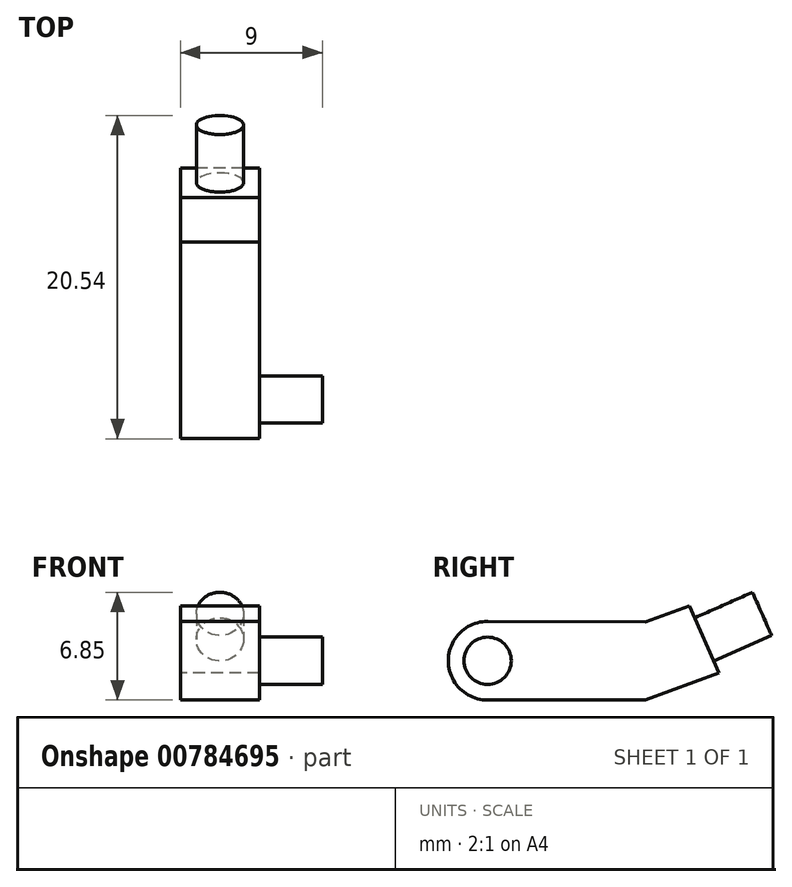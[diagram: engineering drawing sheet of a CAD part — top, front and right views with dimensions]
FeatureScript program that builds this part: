
annotation { "Feature Type Name" : "Feature", "Feature Type Description" : "" }
export const myFeature = defineFeature(function(context is Context, id is Id, definition is map)
    precondition{}
    {
        {
            var Q0;
            Q0=qCreatedBy(makeId("Right.planeOp"),FACE);
            var sketch = newSketch(context, id + "F0", { "sketchPlane" : qUnion([Q0])});
            skLineSegment(sketch, "E0", {"start": v(0, 0) * mm, "end": v(0, -5) * mm});
            skArc(sketch, "E1", {"start": v(0, 0) * mm, "mid": v(-2.5, -2.5) * mm, "end": v(0, -5) * mm});
            skLineSegment(sketch, "E2", {"start": v(0, 0) * mm, "end": v(10, -0.03) * mm});
            skLineSegment(sketch, "E3", {"start": v(0, -5) * mm, "end": v(10, -4.97) * mm});
            skLineSegment(sketch, "E4", {"start": v(10, -4.97) * mm, "end": v(14.7, -3.26) * mm});
            skLineSegment(sketch, "E5", {"start": v(10, -0.03) * mm, "end": v(12.83, 0.98) * mm});
            skLineSegment(sketch, "E6", {"start": v(12.83, 0.98) * mm, "end": v(14.7, -3.26) * mm});
            skSolve(sketch);
        }
        {
            var Q0;
            Q0=makeQuery(id+"F0.imprint","IMPRINT",FACE,{"disambiguationData":[TD([[makeQuery(id+"F0.imprint","IMPRINT",EDGE,{"derivedFrom":sQuery(id+"F0.wireOp",EDGE,"E0")}),1.0]])]});
            var Q1;
            Q1=makeQuery(id+"F0.imprint","IMPRINT",FACE,{"disambiguationData":[TD([[makeQuery(id+"F0.imprint","IMPRINT",EDGE,{"derivedFrom":sQuery(id+"F0.wireOp",EDGE,"E0")}),-1.0]])]});
            extrude(context, id + "F1", {"entities" : qUnion([Q0, Q1]), "depth" : 5 * mm, "offsetDistance" : 25 * mm});
        }
        {
            var Q0;
            Q0=makeQuery(id+"F1.opExtrude","SWEPT_FACE",FACE,{"disambiguationData":[OSD([sQuery(id+"F0.wireOp",EDGE,"E6")])]});
            var sketch = newSketch(context, id + "F2", { "sketchPlane" : qUnion([Q0])});
            skCircle(sketch, "E7", {"center": v(-2.5, -6.6) * mm, "radius": 1.5 * mm});
            skPoint(sketch, "E7.centerSnap0", {"position": v(0, -6.6) * mm});
            skPoint(sketch, "E7.centerSnap1", {"position": v(-2.5, -4.29) * mm});
            skSolve(sketch);
        }
        {
            var Q0;
            Q0=makeQuery(id+"F1.opExtrude","CAP_FACE",FACE,{"disambiguationData":[OSD([sQuery(id+"F0.wireOp",EDGE,"E1"),sQuery(id+"F0.wireOp",EDGE,"E2"),sQuery(id+"F0.wireOp",EDGE,"E3"),sQuery(id+"F0.wireOp",EDGE,"E4"),sQuery(id+"F0.wireOp",EDGE,"E5"),sQuery(id+"F0.wireOp",EDGE,"E6")])],"isStart":false});
            var sketch = newSketch(context, id + "F3", { "sketchPlane" : qUnion([Q0])});
            skCircle(sketch, "E8", {"center": v(0, -2.5) * mm, "radius": 1.5 * mm});
            skSolve(sketch);
        }
        {
            var Q0;
            Q0=makeQuery(id+"F3.imprint","IMPRINT",FACE,{"disambiguationData":[TD([[makeQuery(id+"F3.imprint","IMPRINT",EDGE,{"derivedFrom":sQuery(id+"F3.wireOp",EDGE,"E8")}),1.0]])]});
            extrude(context, id + "F4", {"entities" : qUnion([Q0]), "operationType" : NewBodyOperationType.ADD, "depth" : 4 * mm, "offsetDistance" : 25 * mm});
        }
        {
            var Q0;
            Q0=makeQuery(id+"F2.imprint","IMPRINT",FACE,{"disambiguationData":[TD([[makeQuery(id+"F2.imprint","IMPRINT",EDGE,{"derivedFrom":sQuery(id+"F2.wireOp",EDGE,"E7")}),1.0]])]});
            extrude(context, id + "F5", {"entities" : qUnion([Q0]), "operationType" : NewBodyOperationType.ADD, "depth" : 4 * mm, "offsetDistance" : 25 * mm});
        }
    });
